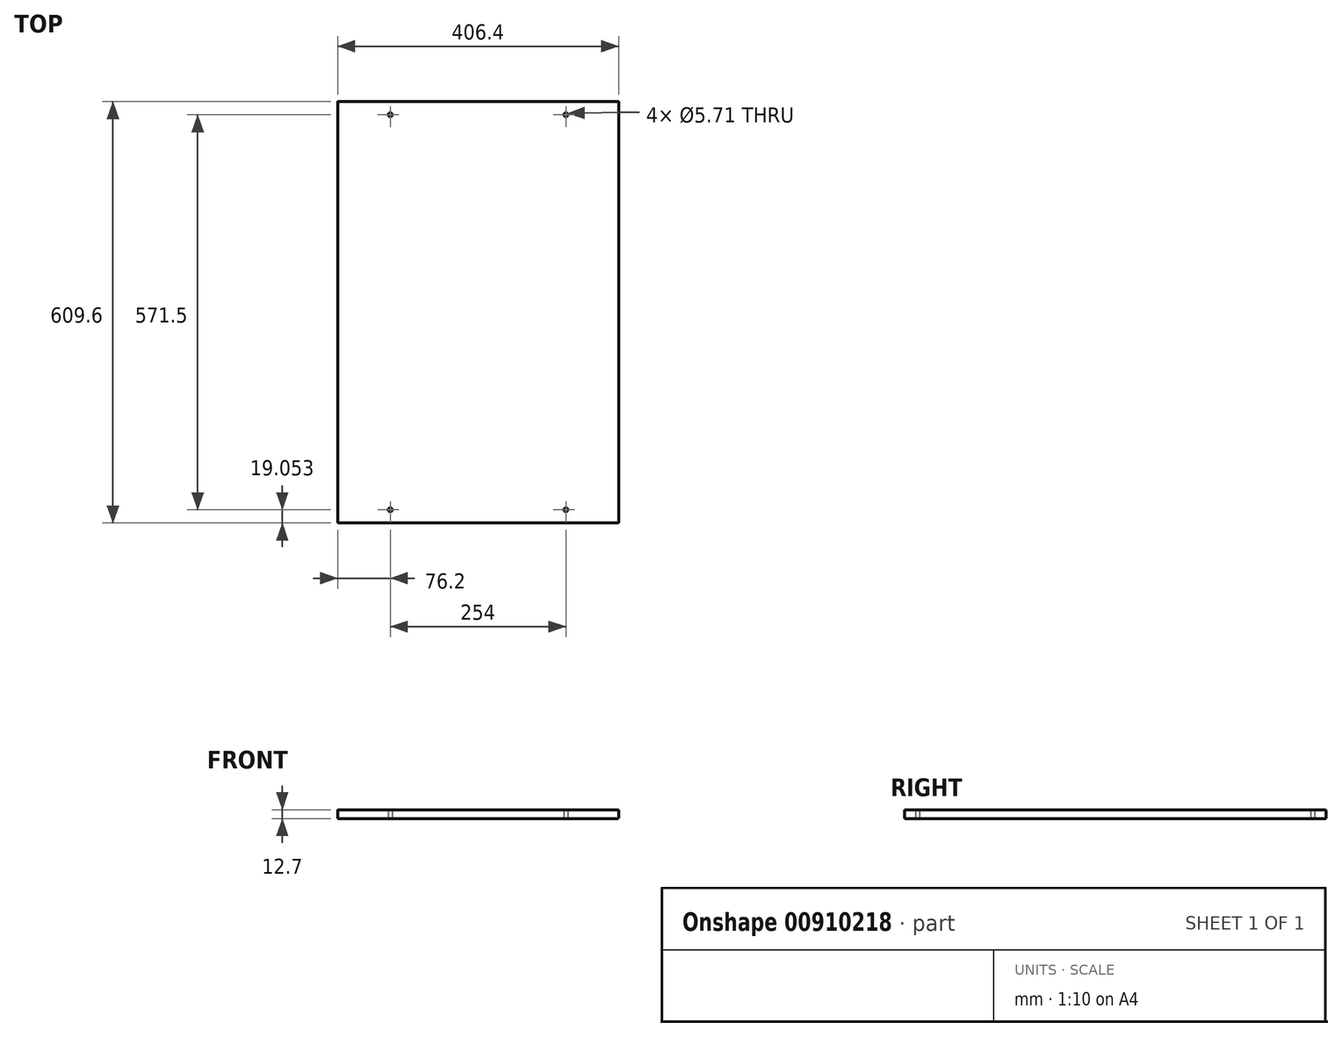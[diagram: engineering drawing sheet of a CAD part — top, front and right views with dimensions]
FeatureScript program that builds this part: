
annotation { "Feature Type Name" : "Feature", "Feature Type Description" : "" }
export const myFeature = defineFeature(function(context is Context, id is Id, definition is map)
    precondition{}
    {
        {
            var Q0;
            Q0=qCreatedBy(makeId("Top.planeOp"),FACE);
            var sketch = newSketch(context, id + "F0", { "sketchPlane" : qUnion([Q0])});
            skLineSegment(sketch, "E0.bottom", {"start": v(-203.2, 302.57) * mm, "end": v(203.2, 302.57) * mm});
            skLineSegment(sketch, "E0.top", {"start": v(-203.2, -307.03) * mm, "end": v(203.2, -307.03) * mm});
            skLineSegment(sketch, "E0.left", {"start": v(-203.2, 302.57) * mm, "end": v(-203.2, -307.03) * mm});
            skLineSegment(sketch, "E0.right", {"start": v(203.2, 302.57) * mm, "end": v(203.2, -307.03) * mm});
            skPoint(sketch, "E0.middle", {"position": v(0, -2.23) * mm});
            skLineSegment(sketch, "E1.bottom", {"start": v(-203.2, 302.57) * mm, "end": v(-158.75, 302.57) * mm});
            skLineSegment(sketch, "E1.top", {"start": v(-203.2, -307.03) * mm, "end": v(-158.75, -307.03) * mm});
            skLineSegment(sketch, "E1.right", {"start": v(-158.75, 302.57) * mm, "end": v(-158.75, -307.03) * mm});
            skLineSegment(sketch, "E2.bottom", {"start": v(203.2, 302.57) * mm, "end": v(158.75, 302.57) * mm});
            skLineSegment(sketch, "E2.top", {"start": v(203.2, -307.03) * mm, "end": v(158.75, -307.03) * mm});
            skLineSegment(sketch, "E2.right", {"start": v(158.75, 302.57) * mm, "end": v(158.75, -307.03) * mm});
            skLineSegment(sketch, "E3.bottom", {"start": v(-203.2, 302.57) * mm, "end": v(-127, 302.57) * mm, "construction": true});
            skLineSegment(sketch, "E3.top", {"start": v(-203.2, 283.52) * mm, "end": v(-127, 283.52) * mm, "construction": true});
            skLineSegment(sketch, "E3.left", {"start": v(-203.2, 302.57) * mm, "end": v(-203.2, 283.52) * mm, "construction": true});
            skLineSegment(sketch, "E3.right", {"start": v(-127, 302.57) * mm, "end": v(-127, 283.52) * mm, "construction": true});
            skLineSegment(sketch, "E4.bottom", {"start": v(203.2, 302.57) * mm, "end": v(127, 302.57) * mm, "construction": true});
            skLineSegment(sketch, "E4.top", {"start": v(203.2, 283.52) * mm, "end": v(127, 283.52) * mm, "construction": true});
            skLineSegment(sketch, "E4.left", {"start": v(203.2, 302.57) * mm, "end": v(203.2, 283.52) * mm, "construction": true});
            skLineSegment(sketch, "E4.right", {"start": v(127, 302.57) * mm, "end": v(127, 283.52) * mm, "construction": true});
            skLineSegment(sketch, "E5.bottom", {"start": v(203.2, -307.03) * mm, "end": v(127, -307.03) * mm, "construction": true});
            skLineSegment(sketch, "E5.top", {"start": v(203.2, -287.98) * mm, "end": v(127, -287.98) * mm, "construction": true});
            skLineSegment(sketch, "E5.left", {"start": v(203.2, -307.03) * mm, "end": v(203.2, -287.98) * mm, "construction": true});
            skLineSegment(sketch, "E5.right", {"start": v(127, -307.03) * mm, "end": v(127, -287.98) * mm, "construction": true});
            skLineSegment(sketch, "E6.bottom", {"start": v(-203.2, -307.03) * mm, "end": v(-127, -307.03) * mm, "construction": true});
            skLineSegment(sketch, "E6.top", {"start": v(-203.2, -287.98) * mm, "end": v(-127, -287.98) * mm, "construction": true});
            skLineSegment(sketch, "E6.left", {"start": v(-203.2, -307.03) * mm, "end": v(-203.2, -287.98) * mm, "construction": true});
            skLineSegment(sketch, "E6.right", {"start": v(-127, -307.03) * mm, "end": v(-127, -287.98) * mm, "construction": true});
            skCircle(sketch, "E7", {"center": v(-127, 283.52) * mm, "radius": 2.86 * mm});
            skCircle(sketch, "E8", {"center": v(127, 283.52) * mm, "radius": 2.86 * mm});
            skCircle(sketch, "E9", {"center": v(-127, -287.98) * mm, "radius": 2.86 * mm});
            skCircle(sketch, "E10", {"center": v(127, -287.98) * mm, "radius": 2.86 * mm});
            skLineSegment(sketch, "E11.bottom", {"start": v(-203.2, 302.57) * mm, "end": v(-184.15, 302.57) * mm, "construction": true});
            skLineSegment(sketch, "E11.top", {"start": v(-203.2, 226.37) * mm, "end": v(-184.15, 226.37) * mm, "construction": true});
            skLineSegment(sketch, "E11.left", {"start": v(-203.2, 302.57) * mm, "end": v(-203.2, 226.37) * mm, "construction": true});
            skLineSegment(sketch, "E11.right", {"start": v(-184.15, 302.57) * mm, "end": v(-184.15, 226.37) * mm, "construction": true});
            skLineSegment(sketch, "E12.bottom", {"start": v(203.2, 302.57) * mm, "end": v(184.15, 302.57) * mm, "construction": true});
            skLineSegment(sketch, "E12.top", {"start": v(203.2, 226.37) * mm, "end": v(184.15, 226.37) * mm, "construction": true});
            skLineSegment(sketch, "E12.left", {"start": v(203.2, 302.57) * mm, "end": v(203.2, 226.37) * mm, "construction": true});
            skLineSegment(sketch, "E12.right", {"start": v(184.15, 302.57) * mm, "end": v(184.15, 226.37) * mm, "construction": true});
            skLineSegment(sketch, "E13.bottom", {"start": v(203.2, -307.03) * mm, "end": v(184.15, -307.03) * mm, "construction": true});
            skLineSegment(sketch, "E13.top", {"start": v(203.2, -230.83) * mm, "end": v(184.15, -230.83) * mm, "construction": true});
            skLineSegment(sketch, "E13.left", {"start": v(203.2, -307.03) * mm, "end": v(203.2, -230.83) * mm, "construction": true});
            skLineSegment(sketch, "E13.right", {"start": v(184.15, -307.03) * mm, "end": v(184.15, -230.83) * mm, "construction": true});
            skLineSegment(sketch, "E14.bottom", {"start": v(-203.2, -307.03) * mm, "end": v(-184.15, -307.03) * mm, "construction": true});
            skLineSegment(sketch, "E14.top", {"start": v(-203.2, -230.83) * mm, "end": v(-184.15, -230.83) * mm, "construction": true});
            skLineSegment(sketch, "E14.left", {"start": v(-203.2, -307.03) * mm, "end": v(-203.2, -230.83) * mm, "construction": true});
            skLineSegment(sketch, "E14.right", {"start": v(-184.15, -307.03) * mm, "end": v(-184.15, -230.83) * mm, "construction": true});
            skCircle(sketch, "E15", {"center": v(-184.15, -230.83) * mm, "radius": 2.86 * mm});
            skCircle(sketch, "E16", {"center": v(184.15, -230.83) * mm, "radius": 2.86 * mm});
            skCircle(sketch, "E17", {"center": v(-184.15, 226.37) * mm, "radius": 2.86 * mm});
            skCircle(sketch, "E18", {"center": v(184.15, 226.37) * mm, "radius": 2.86 * mm});
            skSolve(sketch);
        }
        {
            var Q0;
            {var subQ1=sQuery(id+"F0.wireOp",EDGE,"E0.right");Q0=makeQuery(id+"F0.imprint","IMPRINT",FACE,{"disambiguationData":[TD([[makeQuery(id+"F0.imprint","IMPRINT",EDGE,{"derivedFrom":subQ1}),-1.0]])]});}
            var Q1;
            {var subQ1=sQuery(id+"F0.wireOp",EDGE,"E1.right");Q1=makeQuery(id+"F0.imprint","IMPRINT",FACE,{"disambiguationData":[TD([[makeQuery(id+"F0.imprint","IMPRINT",EDGE,{"derivedFrom":subQ1}),1.0]])]});}
            var Q2;
            {var subQ2=sQuery(id+"F0.wireOp",EDGE,"E0.left");Q2=makeQuery(id+"F0.imprint","IMPRINT",FACE,{"disambiguationData":[TD([[makeQuery(id+"F0.imprint","IMPRINT",EDGE,{"derivedFrom":subQ2}),1.0]])]});}
            var Q3;
            Q3=makeQuery(id+"F0.imprint","IMPRINT",FACE,{"disambiguationData":[TD([[makeQuery(id+"F0.imprint","IMPRINT",EDGE,{"derivedFrom":sQuery(id+"F0.wireOp",EDGE,"E17")}),1.0]])]});
            var Q4;
            Q4=makeQuery(id+"F0.imprint","IMPRINT",FACE,{"disambiguationData":[TD([[makeQuery(id+"F0.imprint","IMPRINT",EDGE,{"derivedFrom":sQuery(id+"F0.wireOp",EDGE,"E15")}),1.0]])]});
            var Q5;
            Q5=makeQuery(id+"F0.imprint","IMPRINT",FACE,{"disambiguationData":[TD([[makeQuery(id+"F0.imprint","IMPRINT",EDGE,{"derivedFrom":sQuery(id+"F0.wireOp",EDGE,"E16")}),1.0]])]});
            var Q6;
            Q6=makeQuery(id+"F0.imprint","IMPRINT",FACE,{"disambiguationData":[TD([[makeQuery(id+"F0.imprint","IMPRINT",EDGE,{"derivedFrom":sQuery(id+"F0.wireOp",EDGE,"E18")}),1.0]])]});
            extrude(context, id + "F1", {"entities" : qUnion([Q0, Q1, Q2, Q3, Q4, Q5, Q6]), "depth" : 12.7 * mm, "offsetDistance" : 25.4 * mm});
        }
        {
            var Q0;
            Q0=makeQuery(id+"F1.opExtrude","CAP_EDGE",EDGE,{"disambiguationData":[OSD([sQuery(id+"F0.wireOp",EDGE,"E0.bottom")])],"isStart":true});
            var Q1;
            Q1=makeQuery(id+"F1.opExtrude","CAP_EDGE",EDGE,{"disambiguationData":[OSD([sQuery(id+"F0.wireOp",EDGE,"E0.left")])],"isStart":true});
            var Q2;
            Q2=makeQuery(id+"F1.opExtrude","CAP_EDGE",EDGE,{"disambiguationData":[OSD([sQuery(id+"F0.wireOp",EDGE,"E0.right")])],"isStart":true});
            var Q3;
            Q3=makeQuery(id+"F1.opExtrude","CAP_EDGE",EDGE,{"disambiguationData":[OSD([sQuery(id+"F0.wireOp",EDGE,"E0.top")])],"isStart":true});
            var Q4;
            Q4=makeQuery(id+"F1.opExtrude","CAP_EDGE",EDGE,{"disambiguationData":[OSD([sQuery(id+"F0.wireOp",EDGE,"E0.right")])],"isStart":false});
            var Q5;
            Q5=makeQuery(id+"F1.opExtrude","CAP_EDGE",EDGE,{"disambiguationData":[OSD([sQuery(id+"F0.wireOp",EDGE,"E0.top")])],"isStart":false});
            var Q6;
            Q6=makeQuery(id+"F1.opExtrude","CAP_EDGE",EDGE,{"disambiguationData":[OSD([sQuery(id+"F0.wireOp",EDGE,"E0.left")])],"isStart":false});
            var Q7;
            Q7=makeQuery(id+"F1.opExtrude","CAP_EDGE",EDGE,{"disambiguationData":[OSD([sQuery(id+"F0.wireOp",EDGE,"E0.bottom")])],"isStart":false});
            fillet(context, id + "F2", {"entities" : qUnion([Q0, Q1, Q2, Q3, Q4, Q5, Q6, Q7]), "radius" : 1.27 * mm, "tangentPropagation" : true, "allowEdgeOverflow" : false});
        }
    });
